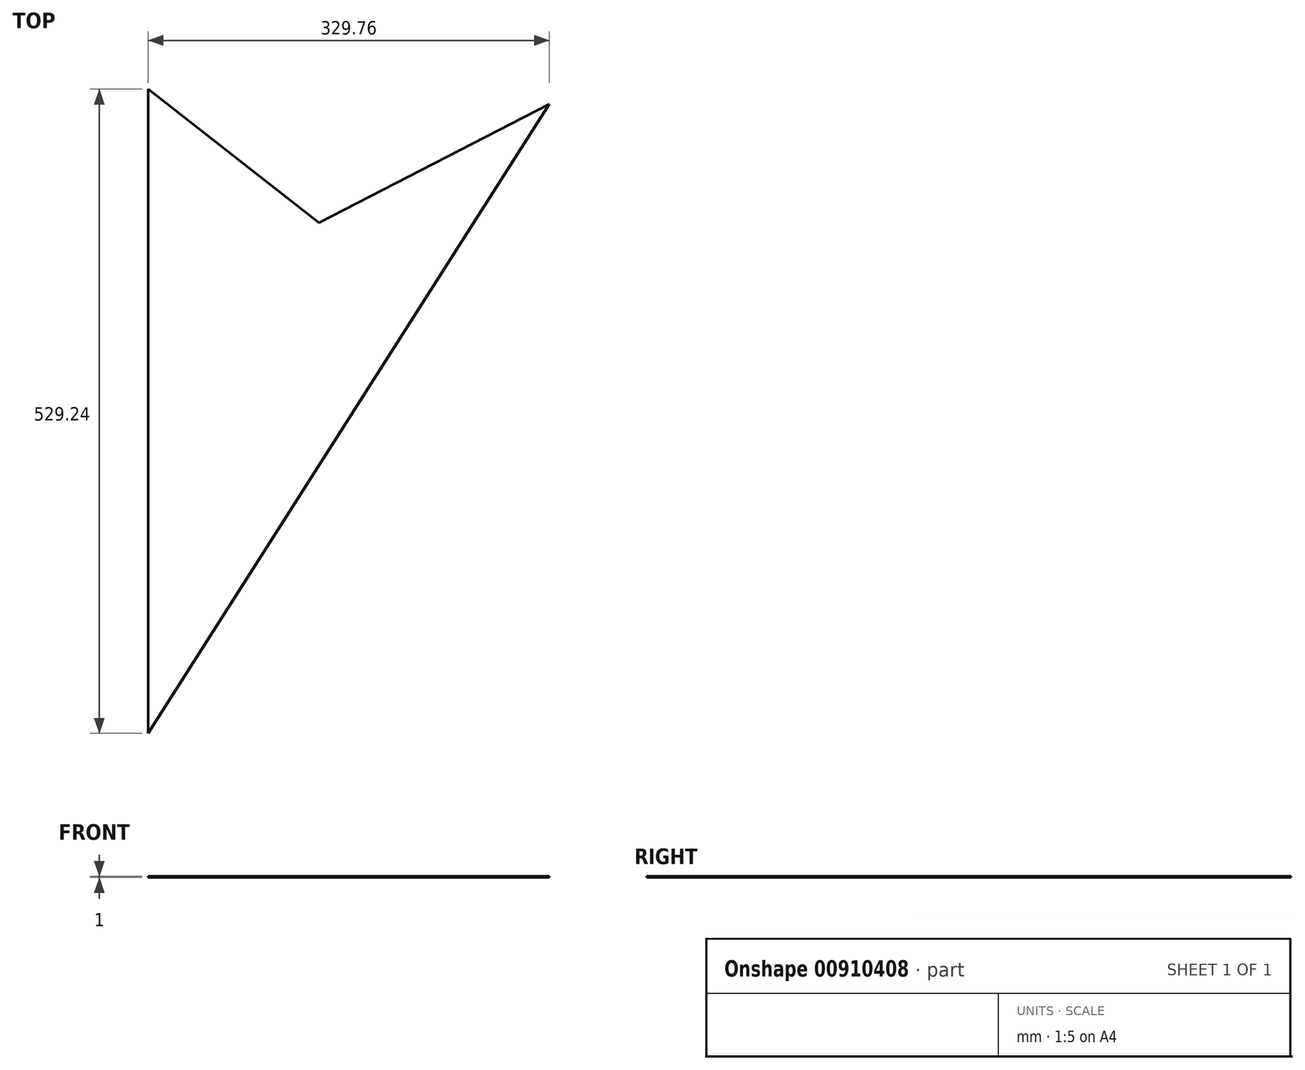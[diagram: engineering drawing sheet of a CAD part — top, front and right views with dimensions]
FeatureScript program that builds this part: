
annotation { "Feature Type Name" : "Feature", "Feature Type Description" : "" }
export const myFeature = defineFeature(function(context is Context, id is Id, definition is map)
    precondition{}
    {
        {
            var Q0;
            Q0=qCreatedBy(makeId("Top.planeOp"),FACE);
            var sketch = newSketch(context, id + "F0", { "sketchPlane" : qUnion([Q0])});
            skLineSegment(sketch, "E0", {"start": v(-162.29, 239.28) * mm, "end": v(-162.29, -289.96) * mm});
            skLineSegment(sketch, "E1", {"start": v(-162.29, -289.96) * mm, "end": v(167.47, 227.07) * mm});
            skLineSegment(sketch, "E2", {"start": v(167.47, 227.07) * mm, "end": v(-21.84, 129.37) * mm});
            skLineSegment(sketch, "E3", {"start": v(-21.84, 129.37) * mm, "end": v(-162.29, 239.28) * mm});
            skSolve(sketch);
        }
        {
            var Q0;
            Q0=makeQuery(id+"F0.imprint","IMPRINT",FACE,{"disambiguationData":[TD([[makeQuery(id+"F0.imprint","IMPRINT",EDGE,{"derivedFrom":sQuery(id+"F0.wireOp",EDGE,"E0")}),1.0]])]});
            extrude(context, id + "F1", {"entities" : qUnion([Q0]), "depth" : 1 * mm, "offsetDistance" : 25 * mm});
        }
    });
